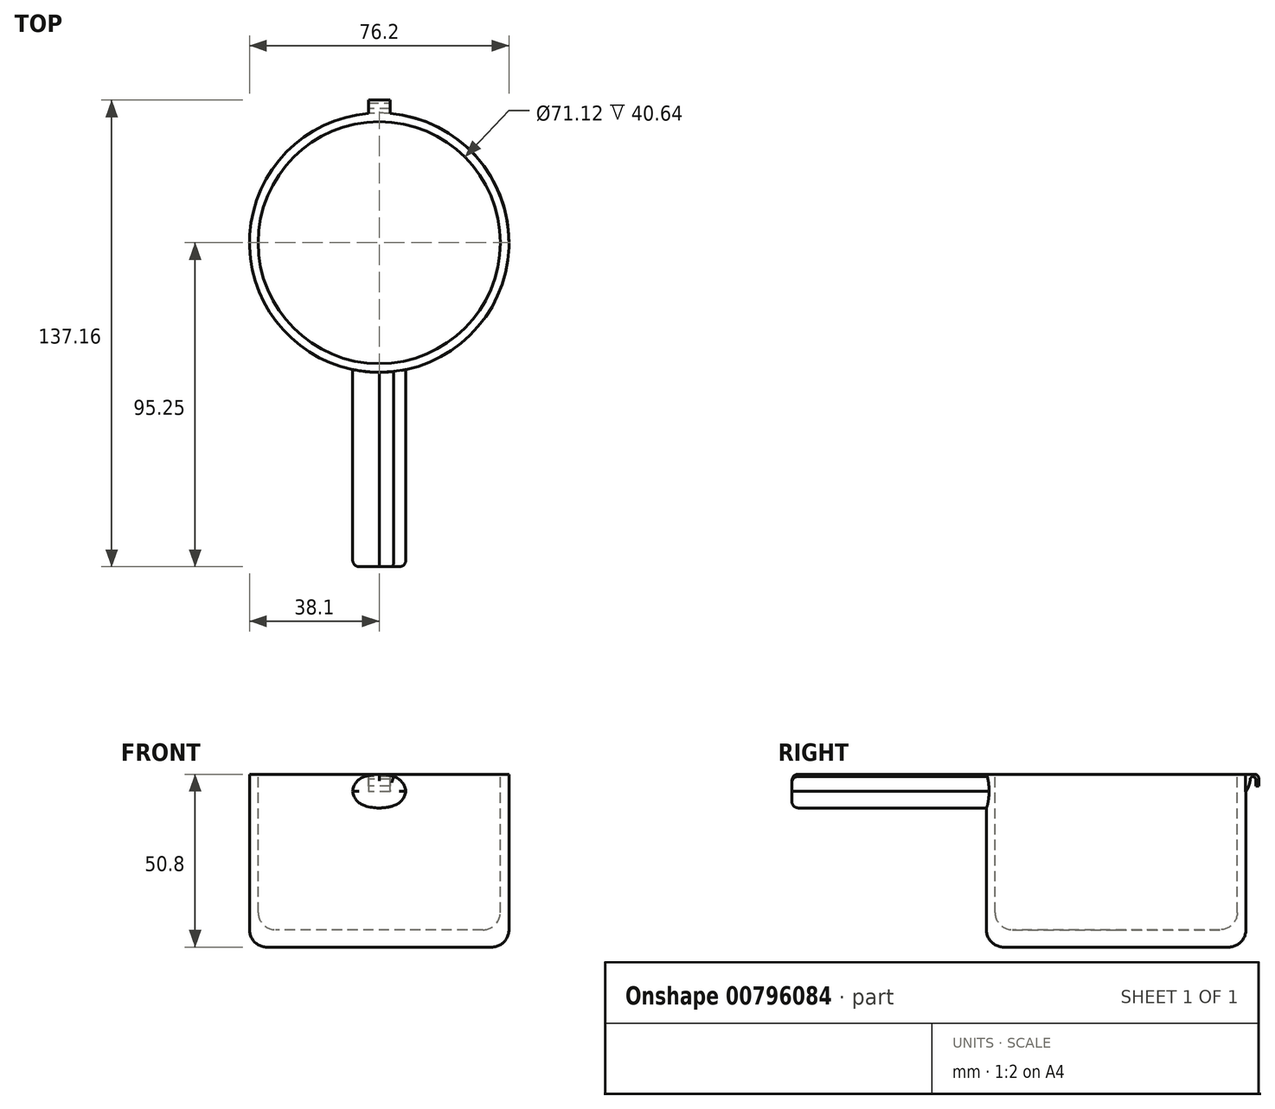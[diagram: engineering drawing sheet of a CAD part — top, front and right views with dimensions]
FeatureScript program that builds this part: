
annotation { "Feature Type Name" : "Feature", "Feature Type Description" : "" }
export const myFeature = defineFeature(function(context is Context, id is Id, definition is map)
    precondition{}
    {
        {
            var Q0;
            Q0=qCreatedBy(makeId("Top.planeOp"),FACE);
            var sketch = newSketch(context, id + "F0", { "sketchPlane" : qUnion([Q0])});
            skCircle(sketch, "E0", {"center": v(0, 0) * mm, "radius": 38.1 * mm});
            skSolve(sketch);
        }
        {
            var Q0;
            Q0 = qSketchRegion(id + "F0", true);
            extrude(context, id + "F1", {"entities" : qUnion([Q0]), "depth" : 50.8 * mm, "offsetDistance" : 25.4 * mm});
        }
        {
            var Q0;
            Q0=makeQuery(id+"F1.opExtrude","CAP_FACE",FACE,{"disambiguationData":[OSD([sQuery(id+"F0.wireOp",EDGE,"E0")])],"isStart":false});
            var sketch = newSketch(context, id + "F2", { "sketchPlane" : qUnion([Q0])});
            skCircle(sketch, "E1", {"center": v(0, 0) * mm, "radius": 35.56 * mm});
            skSolve(sketch);
        }
        {
            var Q0;
            Q0 = qSketchRegion(id + "F2", true);
            extrude(context, id + "F3", {"entities" : qUnion([Q0]), "operationType" : NewBodyOperationType.REMOVE, "oppositeDirection" : true, "depth" : 45.72 * mm, "offsetDistance" : 25.4 * mm});
        }
        {
            var Q0;
            Q0=makeQuery(id+"F3.boolean.opBoolean","COPY",EDGE,{"derivedFrom":makeQuery(id+"F3.opExtrude","CAP_EDGE",EDGE,{"disambiguationData":[OSD([sQuery(id+"F2.wireOp",EDGE,"E1")])],"isStart":false})});
            var Q1;
            Q1=makeQuery(id+"F1.opExtrude","CAP_EDGE",EDGE,{"disambiguationData":[OSD([sQuery(id+"F0.wireOp",EDGE,"E0")])],"isStart":true});
            fillet(context, id + "F4", {"entities" : qUnion([Q0, Q1]), "radius" : 5.08 * mm, "tangentPropagation" : true, "allowEdgeOverflow" : false});
        }
        {
            var Q0;
            Q0=qCreatedBy(makeId("Front.planeOp"),FACE);
            cPlane(context, id + "F5", {"entities" : qUnion([Q0]), "cplaneType" : CPlaneType.OFFSET, "offset" : 38.1 * mm, "width" : 152.4 * mm, "height" : 152.4 * mm});
        }
        {
            var Q0;
            Q0=qCreatedBy(id+"F5.planeOp",FACE);
            var sketch = newSketch(context, id + "F6", { "sketchPlane" : qUnion([Q0])});
            skArc(sketch, "E2", {"start": v(-7.8, 45.84) * mm, "mid": v(-6.68, 43.17) * mm, "end": v(-4.28, 41.55) * mm});
            skArc(sketch, "E3", {"start": v(-4.28, 41.55) * mm, "mid": v(-2.16, 41.06) * mm, "end": v(0, 40.9) * mm});
            skArc(sketch, "E4.MirrorCS", {"start": v(7.8, 45.84) * mm, "mid": v(6.68, 43.17) * mm, "end": v(4.28, 41.55) * mm});
            skArc(sketch, "E5.MirrorCS", {"start": v(4.28, 41.55) * mm, "mid": v(2.16, 41.06) * mm, "end": v(0, 40.9) * mm});
            skPoint(sketch, "E6", {"position": v(0, 45.85) * mm});
            skArc(sketch, "E7.MirrorCS", {"start": v(-4.28, 50.13) * mm, "mid": v(-2.16, 50.63) * mm, "end": v(0, 50.8) * mm});
            skArc(sketch, "E8.MirrorCS", {"start": v(-7.8, 45.84) * mm, "mid": v(-6.68, 48.51) * mm, "end": v(-4.28, 50.13) * mm});
            skArc(sketch, "E9.MirrorCS", {"start": v(7.8, 45.84) * mm, "mid": v(6.68, 48.51) * mm, "end": v(4.28, 50.13) * mm});
            skArc(sketch, "E10", {"start": v(0, 50.8) * mm, "mid": v(2.17, 50.67) * mm, "end": v(4.28, 50.13) * mm});
            skSolve(sketch);
        }
        {
            var Q0;
            Q0=makeQuery(id+"F6.imprint","IMPRINT",FACE,{"disambiguationData":[TD([[makeQuery(id+"F6.imprint","IMPRINT",EDGE,{"derivedFrom":sQuery(id+"F6.wireOp",EDGE,"E2")}),1.0]])]});
            extrude(context, id + "F7", {"entities" : qUnion([Q0]), "operationType" : NewBodyOperationType.ADD, "depth" : 57.15 * mm, "offsetDistance" : 25.4 * mm, "hasSecondDirection" : true, "secondDirectionBound" : SecondDirectionBoundingType.UP_TO_NEXT, "secondDirectionOppositeDirection" : true, "secondDirectionDepth" : 25.4 * mm});
        }
        {
            var Q0;
            {var subQ0=sQuery(id+"F6.wireOp",EDGE,"E5.MirrorCS");var subQ1=sQuery(id+"F6.wireOp",EDGE,"E4.MirrorCS");var subQ2=sQuery(id+"F6.wireOp",EDGE,"E3");var subQ3=sQuery(id+"F6.wireOp",EDGE,"E2");var subQ4=sQuery(id+"F6.wireOp",EDGE,"E7.MirrorCS");var subQ5=sQuery(id+"F6.wireOp",EDGE,"E8.MirrorCS");var subQ6=sQuery(id+"F6.wireOp",EDGE,"E9.MirrorCS");var subQ7=sQuery(id+"F6.wireOp",EDGE,"E10");Q0=makeQuery(id+"F7.opExtrude","CAP_FACE",FACE,{"disambiguationData":[OSD([subQ3,subQ2,subQ1,subQ0,subQ4,subQ5,subQ6,subQ7]),topologyDisambiguationEdgeConnected([makeQuery(id+"F6.imprint","IMPRINT",EDGE,{"derivedFrom":subQ3})])],"isStart":false});}
            fillet(context, id + "F8", {"entities" : qUnion([Q0]), "radius" : 1.9 * mm, "tangentPropagation" : true, "allowEdgeOverflow" : false});
        }
        {
            var Q0;
            Q0=qCreatedBy(makeId("Front.planeOp"),FACE);
            cPlane(context, id + "F9", {"entities" : qUnion([Q0]), "cplaneType" : CPlaneType.OFFSET, "offset" : 38.1 * mm, "oppositeDirection" : true, "width" : 152.4 * mm, "height" : 152.4 * mm});
        }
        {
            var Q0;
            Q0=qCreatedBy(id+"F9.planeOp",FACE);
            var sketch = newSketch(context, id + "F10", { "sketchPlane" : qUnion([Q0])});
            skLineSegment(sketch, "E11.bottom", {"start": v(3.17, 50.8) * mm, "end": v(-3.18, 50.8) * mm});
            skLineSegment(sketch, "E11.top", {"start": v(3.17, 45.72) * mm, "end": v(-3.18, 45.72) * mm});
            skLineSegment(sketch, "E11.left", {"start": v(3.17, 50.8) * mm, "end": v(3.17, 45.72) * mm});
            skLineSegment(sketch, "E11.right", {"start": v(-3.18, 50.8) * mm, "end": v(-3.18, 45.72) * mm});
            skPoint(sketch, "E11.middle", {"position": v(0, 48.26) * mm});
            skSolve(sketch);
        }
        {
            var Q0;
            Q0 = qSketchRegion(id + "F10", true);
            extrude(context, id + "F11", {"entities" : qUnion([Q0]), "operationType" : NewBodyOperationType.ADD, "oppositeDirection" : true, "depth" : 1.27 * mm, "offsetDistance" : 25.4 * mm, "hasSecondDirection" : true, "secondDirectionBound" : SecondDirectionBoundingType.UP_TO_NEXT, "secondDirectionOppositeDirection" : false, "secondDirectionDepth" : 25.4 * mm});
        }
        {
            var Q0;
            {var subQ0=sQuery(id+"F10.wireOp",EDGE,"E11.bottom");var subQ1=sQuery(id+"F10.wireOp",EDGE,"E11.top");var subQ2=sQuery(id+"F10.wireOp",EDGE,"E11.left");var subQ3=sQuery(id+"F10.wireOp",EDGE,"E11.right");Q0=makeQuery(id+"F11.opExtrude","CAP_FACE",FACE,{"disambiguationData":[OSD([subQ0,subQ1,subQ2,subQ3]),topologyDisambiguationEdgeConnected([makeQuery(id+"F10.imprint","IMPRINT",EDGE,{"derivedFrom":subQ0})])],"isStart":false});}
            var sketch = newSketch(context, id + "F12", { "sketchPlane" : qUnion([Q0])});
            skLineSegment(sketch, "E12.bottom", {"start": v(-3.17, 50.8) * mm, "end": v(3.17, 50.8) * mm});
            skLineSegment(sketch, "E12.left", {"start": v(-3.17, 50.8) * mm, "end": v(-3.17, 49.26) * mm});
            skLineSegment(sketch, "E12.right", {"start": v(3.17, 50.8) * mm, "end": v(3.17, 49.26) * mm});
            skPoint(sketch, "E12.middle", {"position": v(0, 50.03) * mm});
            skLineSegment(sketch, "E13", {"start": v(-3.17, 49.26) * mm, "end": v(3.17, 49.26) * mm});
            skSolve(sketch);
        }
        {
            var Q0;
            Q0 = qSketchRegion(id + "F12", true);
            extrude(context, id + "F13", {"entities" : qUnion([Q0]), "operationType" : NewBodyOperationType.ADD, "depth" : 2.54 * mm, "offsetDistance" : 25.4 * mm});
        }
        {
            var Q0;
            Q0=makeQuery(id+"F13.opExtrude","SWEPT_FACE",FACE,{"disambiguationData":[OSD([sQuery(id+"F12.wireOp",EDGE,"E13")])]});
            var sketch = newSketch(context, id + "F14", { "sketchPlane" : qUnion([Q0])});
            skLineSegment(sketch, "E14.bottom", {"start": v(-3.18, -41.9) * mm, "end": v(3.18, -41.9) * mm});
            skLineSegment(sketch, "E14.top", {"start": v(-3.18, -41) * mm, "end": v(3.18, -41) * mm});
            skLineSegment(sketch, "E14.left", {"start": v(-3.18, -41.9) * mm, "end": v(-3.18, -41) * mm});
            skLineSegment(sketch, "E14.right", {"start": v(3.17, -41.9) * mm, "end": v(3.17, -41) * mm});
            skPoint(sketch, "E14.middle", {"position": v(0, -41.46) * mm});
            skPoint(sketch, "E14.middle.positionSnap0", {"position": v(0, -41.9) * mm});
            skPoint(sketch, "E14.centerSnap0", {"position": v(0, -41.9) * mm});
            skSolve(sketch);
        }
        {
            var Q0;
            Q0 = qSketchRegion(id + "F14", true);
            extrude(context, id + "F15", {"entities" : qUnion([Q0]), "operationType" : NewBodyOperationType.ADD, "depth" : 1.9 * mm, "offsetDistance" : 25.4 * mm});
        }
        {
            var Q0;
            Q0=makeQuery(id+"F15.boolean.opBoolean","MERGE",FACE,{"derivedFrom":[makeQuery(id+"F13.boolean.opBoolean","MERGE",FACE,{"derivedFrom":[makeQuery(id+"F11.opExtrude","SWEPT_FACE",FACE,{"disambiguationData":[OSD([sQuery(id+"F10.wireOp",EDGE,"E11.right")])]}),makeQuery(id+"F13.opExtrude","SWEPT_FACE",FACE,{"disambiguationData":[OSD([sQuery(id+"F12.wireOp",EDGE,"E12.right")])]})]}),makeQuery(id+"F15.opExtrude","SWEPT_FACE",FACE,{"disambiguationData":[OSD([sQuery(id+"F14.wireOp",EDGE,"E14.left")])]})]});
            var sketch = newSketch(context, id + "F16", { "sketchPlane" : qUnion([Q0])});
            skCircle(sketch, "E15", {"center": v(-40.19, 49.26) * mm, "radius": 0.82 * mm});
            skSolve(sketch);
        }
        {
            var Q0;
            Q0 = qSketchRegion(id + "F16", true);
            extrude(context, id + "F17", {"entities" : qUnion([Q0]), "operationType" : NewBodyOperationType.REMOVE, "endBound" : BoundingType.THROUGH_ALL, "oppositeDirection" : true, "depth" : 25.4 * mm, "offsetDistance" : 25.4 * mm});
        }
        {
            var Q0;
            Q0=makeQuery(id+"F13.opExtrude","CAP_EDGE",EDGE,{"disambiguationData":[OSD([sQuery(id+"F12.wireOp",EDGE,"E12.bottom")])],"isStart":false});
            fillet(context, id + "F18", {"entities" : qUnion([Q0]), "radius" : 1.27 * mm, "tangentPropagation" : true, "allowEdgeOverflow" : false});
        }
        {
            var Q0;
            {var subQ0=sQuery(id+"F10.wireOp",EDGE,"E11.top");Q0=makeQuery(id+"F11.opExtrude","CAP_EDGE",EDGE,{"disambiguationData":[OSD([subQ0]),topologyDisambiguationEdgeConnected([makeQuery(id+"F10.imprint","IMPRINT",EDGE,{"derivedFrom":sQuery(id+"F10.wireOp",EDGE,"E11.bottom")})])],"isStart":false});}
            fillet(context, id + "F19", {"entities" : qUnion([Q0]), "radius" : 6.35 * mm, "tangentPropagation" : true, "allowEdgeOverflow" : false});
        }
    });
